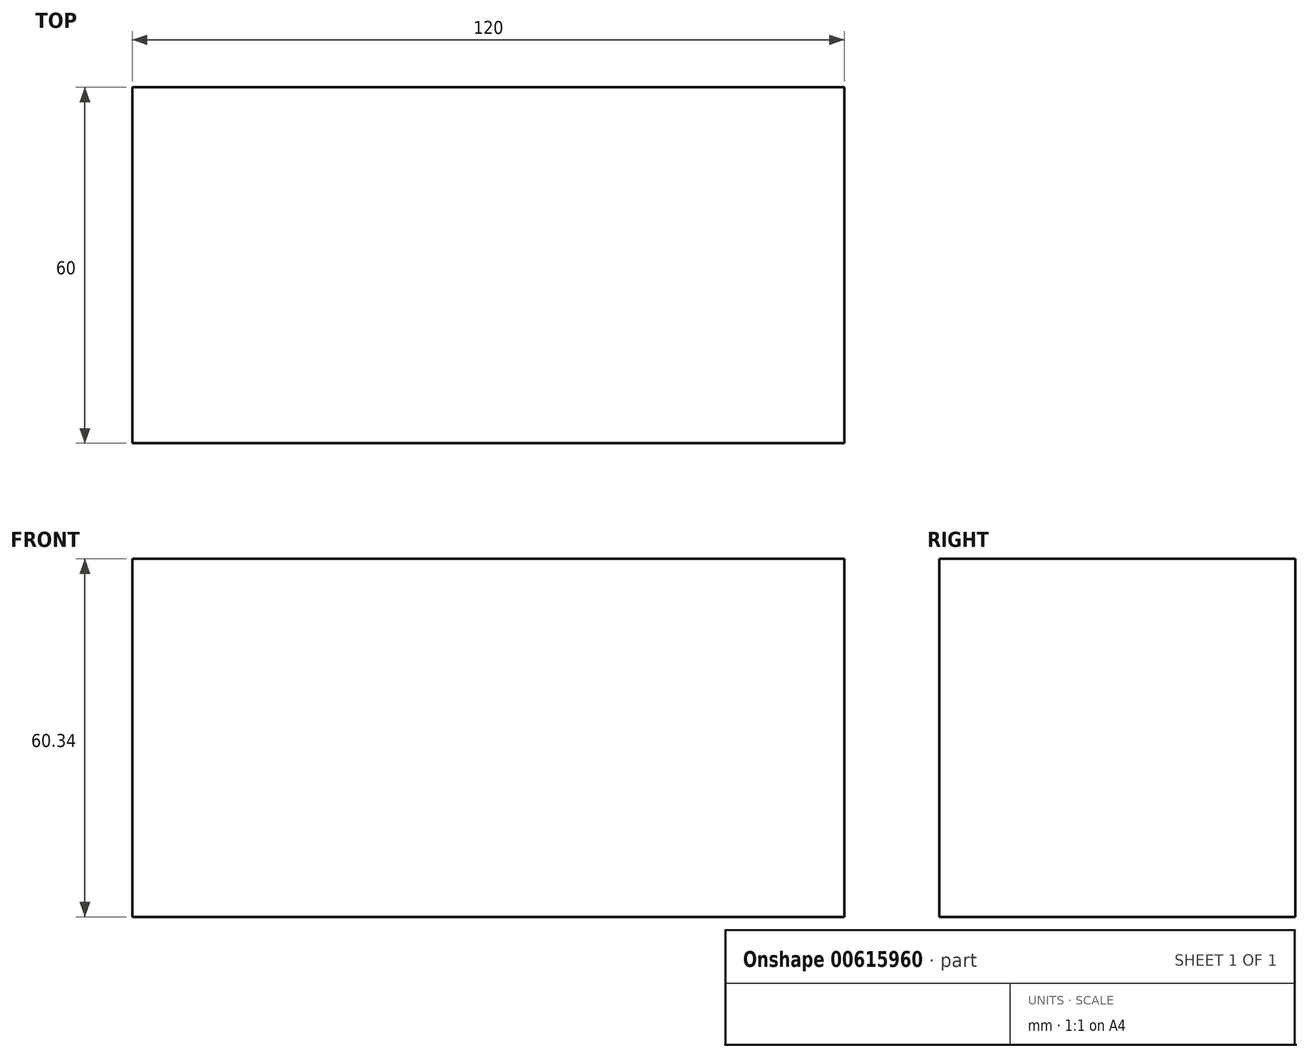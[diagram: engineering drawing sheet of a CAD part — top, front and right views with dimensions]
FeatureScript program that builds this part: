
annotation { "Feature Type Name" : "Feature", "Feature Type Description" : "" }
export const myFeature = defineFeature(function(context is Context, id is Id, definition is map)
    precondition{}
    {
        {
            var Q0;
            Q0=qCreatedBy(makeId("Front.planeOp"),FACE);
            var sketch = newSketch(context, id + "F0", { "sketchPlane" : qUnion([Q0])});
            skLineSegment(sketch, "E0.bottom", {"start": v(-60, 30.17) * mm, "end": v(60, 30.17) * mm});
            skLineSegment(sketch, "E0.top", {"start": v(-60, -30.17) * mm, "end": v(60, -30.17) * mm});
            skLineSegment(sketch, "E0.left", {"start": v(-60, 30.17) * mm, "end": v(-60, -30.17) * mm});
            skLineSegment(sketch, "E0.right", {"start": v(60, 30.17) * mm, "end": v(60, -30.17) * mm});
            skPoint(sketch, "E0.middle", {"position": v(0, 0) * mm});
            skSolve(sketch);
        }
        {
            var Q0;
            Q0=makeQuery(id+"F0.imprint","IMPRINT",FACE,{"disambiguationData":[TD([[makeQuery(id+"F0.imprint","IMPRINT",EDGE,{"derivedFrom":sQuery(id+"F0.wireOp",EDGE,"E0.bottom")}),-1.0]])]});
            extrude(context, id + "F1", {"entities" : qUnion([Q0]), "endBound" : BoundingType.SYMMETRIC, "depth" : 60 * mm, "offsetDistance" : 25 * mm});
        }
    });
